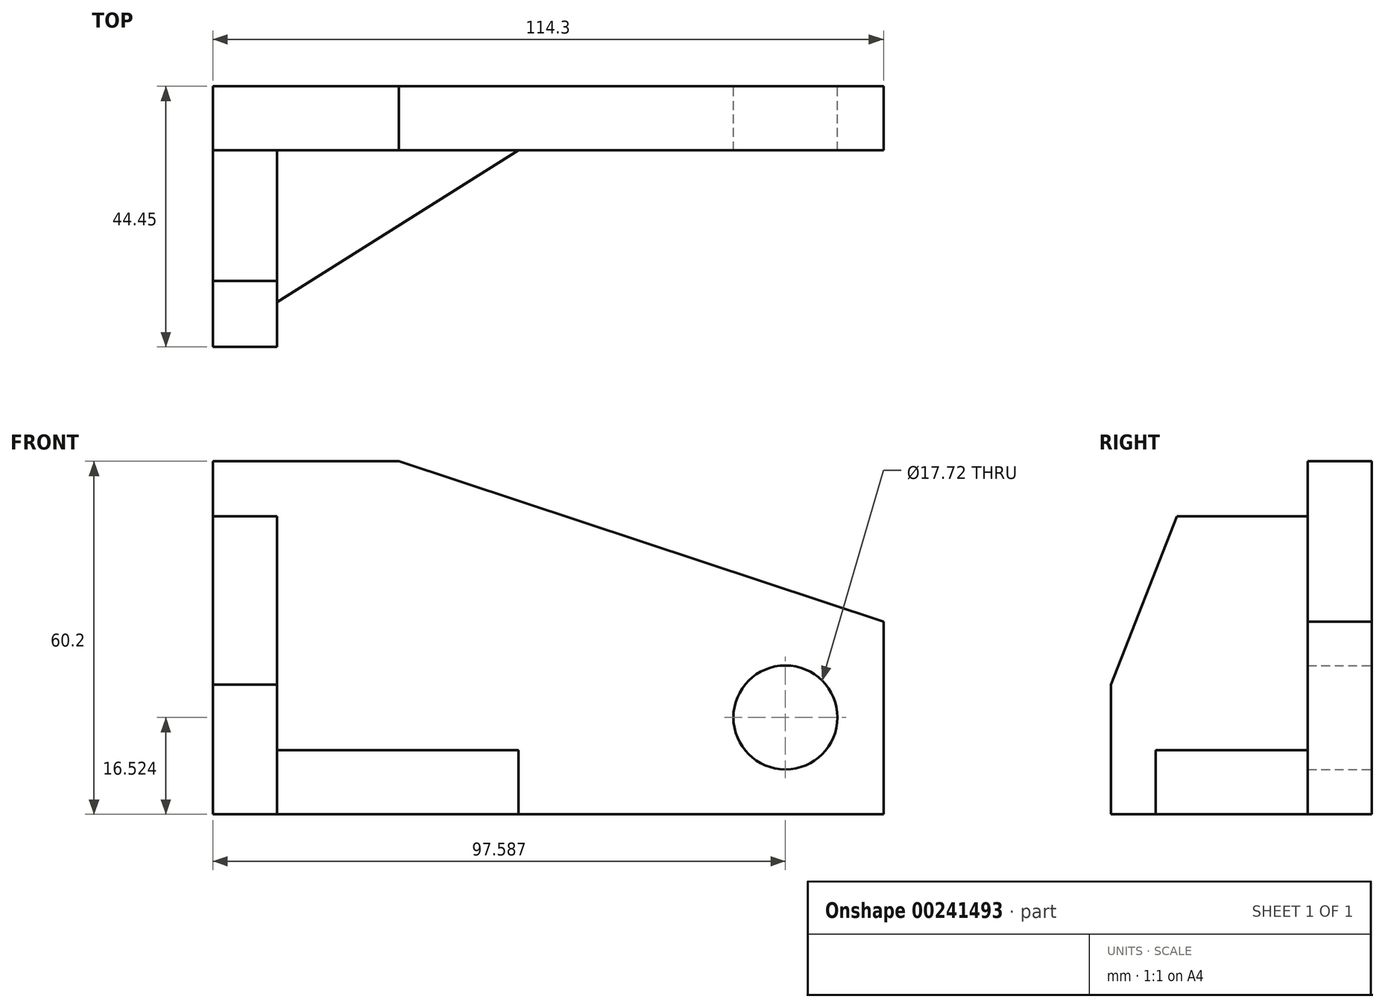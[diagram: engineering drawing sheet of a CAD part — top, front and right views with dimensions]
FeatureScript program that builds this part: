
annotation { "Feature Type Name" : "Feature", "Feature Type Description" : "" }
export const myFeature = defineFeature(function(context is Context, id is Id, definition is map)
    precondition{}
    {
        {
            var Q0;
            Q0=qCreatedBy(makeId("Front.planeOp"),FACE);
            var sketch = newSketch(context, id + "F0", { "sketchPlane" : qUnion([Q0])});
            skLineSegment(sketch, "E0", {"start": v(0, 60.2) * mm, "end": v(0, 0) * mm});
            skLineSegment(sketch, "E1", {"start": v(0, 0) * mm, "end": v(114.3, 0) * mm});
            skLineSegment(sketch, "E2", {"start": v(0, 60.2) * mm, "end": v(31.75, 60.2) * mm});
            skLineSegment(sketch, "E3", {"start": v(31.75, 60.2) * mm, "end": v(114.3, 32.89) * mm});
            skLineSegment(sketch, "E4", {"start": v(114.3, 32.89) * mm, "end": v(114.3, 0) * mm});
            skSolve(sketch);
        }
        {
            var Q0;
            Q0 = qSketchRegion(id + "F0", true);
            extrude(context, id + "F1", {"entities" : qUnion([Q0]), "depth" : 10.92 * mm});
        }
        {
            var Q0;
            Q0=qCreatedBy(makeId("Right.planeOp"),FACE);
            var sketch = newSketch(context, id + "F2", { "sketchPlane" : qUnion([Q0])});
            skLineSegment(sketch, "E5", {"start": v(0, 0) * mm, "end": v(0, 50.8) * mm});
            skLineSegment(sketch, "E6", {"start": v(0, 50.8) * mm, "end": v(-33.22, 50.8) * mm});
            skLineSegment(sketch, "E7", {"start": v(-33.22, 50.8) * mm, "end": v(-44.45, 22.1) * mm});
            skLineSegment(sketch, "E8", {"start": v(-44.45, 22.1) * mm, "end": v(-44.45, 0) * mm});
            skLineSegment(sketch, "E9", {"start": v(-44.45, 0) * mm, "end": v(0, 0) * mm});
            skLineSegment(sketch, "E10", {"start": v(0, 50.8) * mm, "end": v(0, 0) * mm});
            skSolve(sketch);
        }
        {
            var Q0;
            Q0 = qSketchRegion(id + "F2", true);
            extrude(context, id + "F3", {"entities" : qUnion([Q0]), "operationType" : NewBodyOperationType.ADD, "depth" : 10.92 * mm});
        }
        {
            var Q0;
            Q0=qCreatedBy(makeId("Top.planeOp"),FACE);
            var sketch = newSketch(context, id + "F4", { "sketchPlane" : qUnion([Q0])});
            skLineSegment(sketch, "E11", {"start": v(0, -10.64) * mm, "end": v(52.58, -10.64) * mm});
            skLineSegment(sketch, "E12", {"start": v(0, -10.64) * mm, "end": v(0, -43.69) * mm});
            skLineSegment(sketch, "E13", {"start": v(0, -43.69) * mm, "end": v(52.58, -10.64) * mm});
            skSolve(sketch);
        }
        {
            var Q0;
            Q0 = qSketchRegion(id + "F4", true);
            extrude(context, id + "F5", {"entities" : qUnion([Q0]), "operationType" : NewBodyOperationType.ADD, "depth" : 10.92 * mm});
        }
        {
            var Q0;
            Q0=qCreatedBy(makeId("Front.planeOp"),FACE);
            var sketch = newSketch(context, id + "F6", { "sketchPlane" : qUnion([Q0])});
            skCircle(sketch, "E14", {"center": v(97.59, 16.52) * mm, "radius": 8.86 * mm});
            skSolve(sketch);
        }
        {
            var Q0;
            Q0 = qSketchRegion(id + "F6", true);
            extrude(context, id + "F7", {"entities" : qUnion([Q0]), "operationType" : NewBodyOperationType.REMOVE, "depth" : 88.65 * mm});
        }
    });
